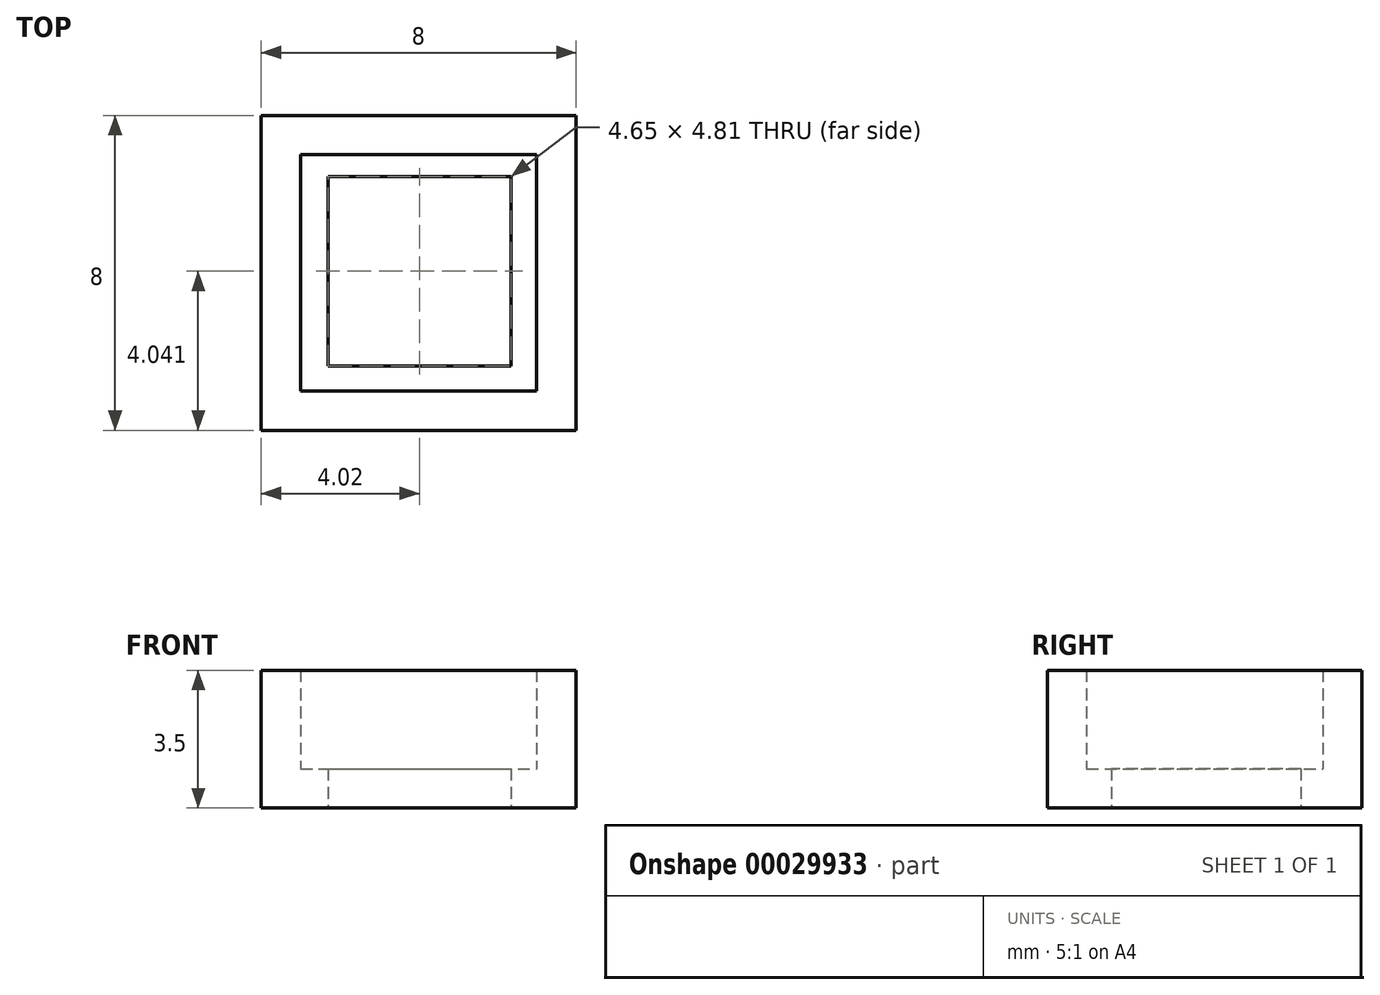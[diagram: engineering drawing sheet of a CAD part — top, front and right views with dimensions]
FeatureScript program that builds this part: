
annotation { "Feature Type Name" : "Feature", "Feature Type Description" : "" }
export const myFeature = defineFeature(function(context is Context, id is Id, definition is map)
    precondition{}
    {
        {
            var Q0;
            Q0=qCreatedBy(makeId("Top.planeOp"),FACE);
            var sketch = newSketch(context, id + "F0", { "sketchPlane" : qUnion([Q0])});
            skLineSegment(sketch, "E0.bottom", {"start": v(0, 0) * mm, "end": v(8, 0) * mm});
            skLineSegment(sketch, "E0.top", {"start": v(0, -8) * mm, "end": v(8, -8) * mm});
            skLineSegment(sketch, "E0.left", {"start": v(0, 0) * mm, "end": v(0, -8) * mm});
            skLineSegment(sketch, "E0.right", {"start": v(8, 0) * mm, "end": v(8, -8) * mm});
            skLineSegment(sketch, "E1", {"start": v(1, -1) * mm, "end": v(7, -1) * mm});
            skLineSegment(sketch, "E2", {"start": v(7, -1) * mm, "end": v(7, -7) * mm});
            skLineSegment(sketch, "E3", {"start": v(7, -7) * mm, "end": v(1, -7) * mm});
            skLineSegment(sketch, "E4", {"start": v(1, -7) * mm, "end": v(1, -1) * mm});
            skLineSegment(sketch, "E5.bottom", {"start": v(1.7, -1.55) * mm, "end": v(6.34, -1.55) * mm});
            skLineSegment(sketch, "E5.top", {"start": v(1.7, -6.36) * mm, "end": v(6.34, -6.36) * mm});
            skLineSegment(sketch, "E5.left", {"start": v(1.7, -1.55) * mm, "end": v(1.7, -6.36) * mm});
            skLineSegment(sketch, "E5.right", {"start": v(6.34, -1.55) * mm, "end": v(6.34, -6.36) * mm});
            skSolve(sketch);
        }
        {
            var Q0;
            Q0=makeQuery(id+"F0.imprint","IMPRINT",FACE,{"disambiguationData":[TD([[makeQuery(id+"F0.imprint","IMPRINT",EDGE,{"derivedFrom":sQuery(id+"F0.wireOp",EDGE,"E0.bottom")}),-1.0]])]});
            extrude(context, id + "F1", {"entities" : qUnion([Q0]), "depth" : 3.5 * mm});
        }
        {
            var Q0;
            Q0=makeQuery(id+"F0.imprint","IMPRINT",FACE,{"disambiguationData":[TD([[makeQuery(id+"F0.imprint","IMPRINT",EDGE,{"derivedFrom":sQuery(id+"F0.wireOp",EDGE,"E1")}),-1.0]])]});
            extrude(context, id + "F2", {"entities" : qUnion([Q0]), "operationType" : NewBodyOperationType.ADD, "depth" : 1 * mm});
        }
    });
